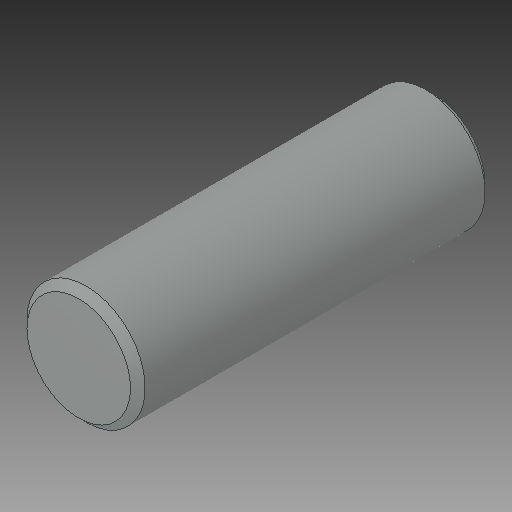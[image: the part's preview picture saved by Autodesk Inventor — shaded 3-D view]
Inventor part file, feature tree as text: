
AUTODESK INVENTOR PART (.ipt)
format: ipt  version: 2018 (Build 220112000, 112)  size: 97,792 bytes
history: native  units: in
note: dims shown in document units (in); Inventor stores cm internally (conversion verified against a paired STEP export)
features: chamfer x1
ambient origin geometry x8: Origin, YZ Plane, XZ Plane, XY Plane, X Axis, Y Axis, Z Axis, Center Point
bodies: Solid1 (feature_tree)
feature tree (1):
  chamfer  "Chamfer1"  [1 undecoded]
note: 1 required parameter value undecoded (feature->parameter linkage not recoverable at this tier; creation-order binding heuristic only, values carry confidence <= 0.55)
